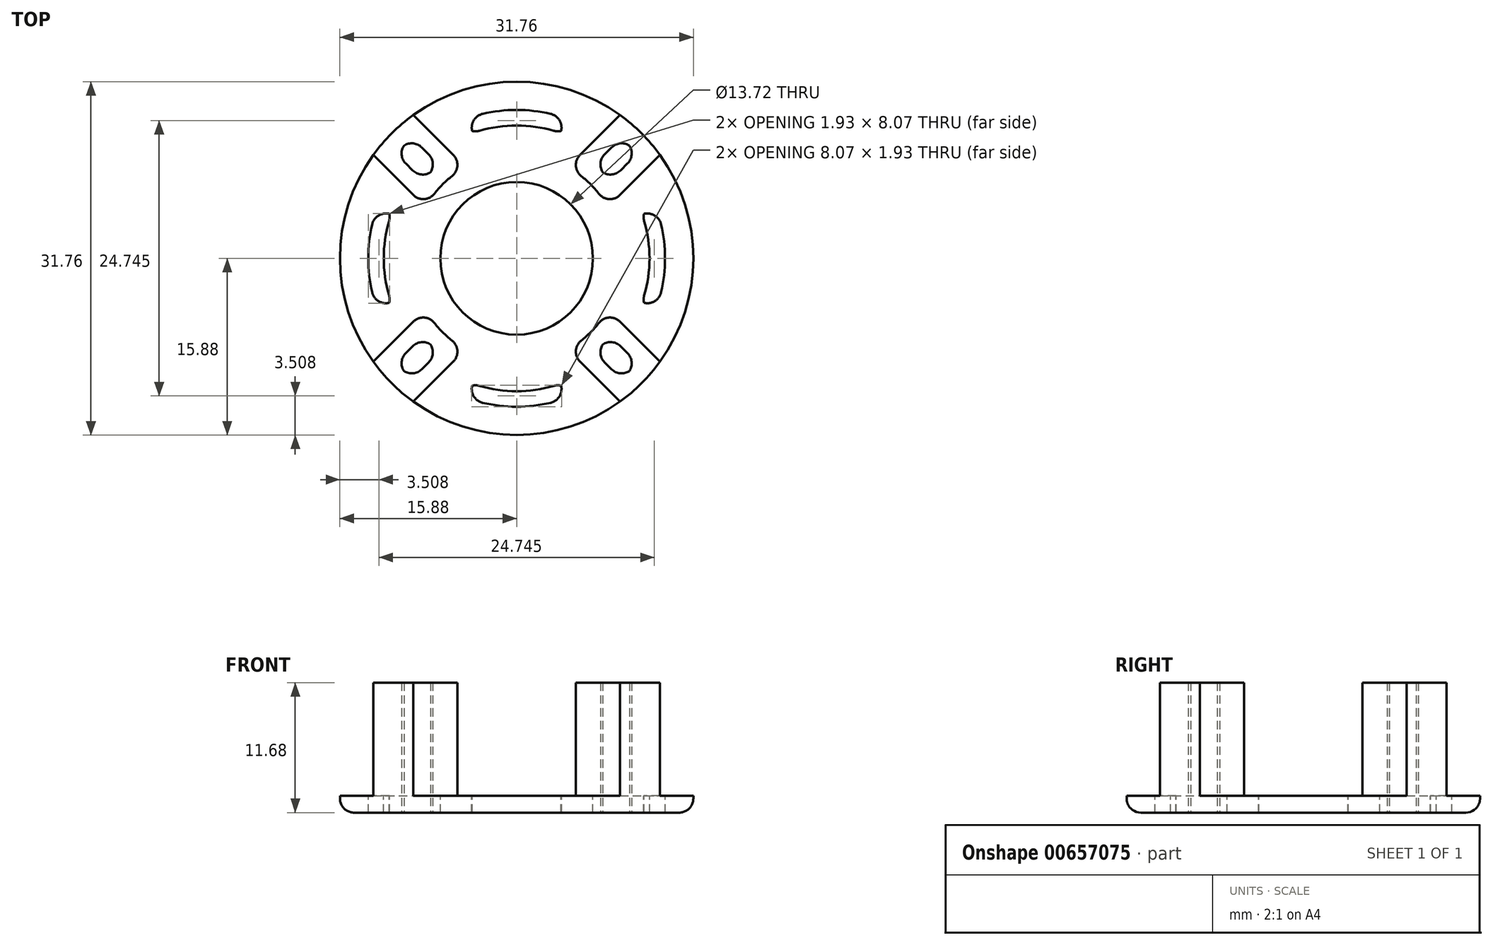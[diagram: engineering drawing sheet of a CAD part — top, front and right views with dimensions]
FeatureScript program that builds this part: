
annotation { "Feature Type Name" : "Feature", "Feature Type Description" : "" }
export const myFeature = defineFeature(function(context is Context, id is Id, definition is map)
    precondition{}
    {
        {
            var Q0;
            Q0=qCreatedBy(makeId("Top.planeOp"),FACE);
            var sketch = newSketch(context, id + "F0", { "sketchPlane" : qUnion([Q0])});
            skCircle(sketch, "E0", {"center": v(0, 0) * mm, "radius": 15.88 * mm});
            skSolve(sketch);
        }
        {
            var Q0;
            Q0=qSketchRegion(id+"F0",true);
            extrude(context, id + "F1", {"entities" : qUnion([Q0]), "depth" : 1.52 * mm, "offsetDistance" : 25.4 * mm});
        }
        {
            var Q0;
            Q0=makeQuery(id+"F1.opExtrude","CAP_FACE",FACE,{"disambiguationData":[OSD([sQuery(id+"F0.wireOp",EDGE,"E0")])],"isStart":false});
            var sketch = newSketch(context, id + "F2", { "sketchPlane" : qUnion([Q0])});
            skArc(sketch, "E1", {"start": v(-8.2, 4.6) * mm, "mid": v(-9.4, 0) * mm, "end": v(-8.2, -4.6) * mm, "construction": true});
            skArc(sketch, "E2", {"start": v(-4.6, 8.2) * mm, "mid": v(-6.65, 6.65) * mm, "end": v(-8.2, 4.6) * mm});
            skArc(sketch, "E3", {"start": v(4.6, 8.2) * mm, "mid": v(0, 9.4) * mm, "end": v(-4.6, 8.2) * mm, "construction": true});
            skArc(sketch, "E4", {"start": v(8.2, 4.6) * mm, "mid": v(6.65, 6.65) * mm, "end": v(4.6, 8.2) * mm});
            skArc(sketch, "E5", {"start": v(8.2, -4.6) * mm, "mid": v(9.4, 0) * mm, "end": v(8.2, 4.6) * mm, "construction": true});
            skArc(sketch, "E6", {"start": v(4.6, -8.2) * mm, "mid": v(6.65, -6.65) * mm, "end": v(8.2, -4.6) * mm});
            skArc(sketch, "E7", {"start": v(-4.6, -8.2) * mm, "mid": v(0, -9.4) * mm, "end": v(4.6, -8.2) * mm, "construction": true});
            skArc(sketch, "E8", {"start": v(-8.2, -4.6) * mm, "mid": v(-6.65, -6.65) * mm, "end": v(-4.6, -8.2) * mm});
            skArc(sketch, "E9", {"start": v(-12.88, -9.28) * mm, "mid": v(-11.23, -11.23) * mm, "end": v(-9.28, -12.88) * mm});
            skArc(sketch, "E10", {"start": v(-12.88, 9.28) * mm, "mid": v(-15.87, 0) * mm, "end": v(-12.88, -9.28) * mm, "construction": true});
            skArc(sketch, "E11", {"start": v(-9.28, 12.88) * mm, "mid": v(-11.23, 11.23) * mm, "end": v(-12.88, 9.28) * mm});
            skArc(sketch, "E12", {"start": v(9.28, 12.88) * mm, "mid": v(0, 15.88) * mm, "end": v(-9.28, 12.88) * mm, "construction": true});
            skArc(sketch, "E13", {"start": v(12.88, 9.28) * mm, "mid": v(11.23, 11.23) * mm, "end": v(9.28, 12.88) * mm});
            skArc(sketch, "E14", {"start": v(12.88, -9.28) * mm, "mid": v(15.88, 0) * mm, "end": v(12.88, 9.28) * mm, "construction": true});
            skArc(sketch, "E15", {"start": v(9.28, -12.88) * mm, "mid": v(11.23, -11.23) * mm, "end": v(12.88, -9.28) * mm});
            skArc(sketch, "E16", {"start": v(-9.28, -12.88) * mm, "mid": v(0, -15.88) * mm, "end": v(9.28, -12.88) * mm, "construction": true});
            skLineSegment(sketch, "E17", {"start": v(-12.88, 9.28) * mm, "end": v(-8.2, 4.6) * mm});
            skLineSegment(sketch, "E18", {"start": v(-4.6, 8.2) * mm, "end": v(-9.28, 12.88) * mm});
            skLineSegment(sketch, "E19", {"start": v(4.6, 8.2) * mm, "end": v(9.28, 12.88) * mm});
            skLineSegment(sketch, "E20", {"start": v(8.2, 4.6) * mm, "end": v(12.88, 9.28) * mm});
            skLineSegment(sketch, "E21", {"start": v(4.6, -8.2) * mm, "end": v(9.28, -12.88) * mm});
            skLineSegment(sketch, "E22", {"start": v(8.2, -4.6) * mm, "end": v(12.88, -9.28) * mm});
            skLineSegment(sketch, "E23", {"start": v(-9.28, -12.88) * mm, "end": v(-4.6, -8.2) * mm});
            skLineSegment(sketch, "E24", {"start": v(-12.88, -9.28) * mm, "end": v(-8.2, -4.6) * mm});
            skLineSegment(sketch, "E25", {"start": v(8.2, 4.6) * mm, "end": v(0, 4.6) * mm, "construction": true});
            skLineSegment(sketch, "E26", {"start": v(4.6, 8.2) * mm, "end": v(4.6, 0) * mm, "construction": true});
            skSolve(sketch);
        }
        {
            var Q0;
            Q0 = qSketchRegion(id + "F2", true);
            extrude(context, id + "F3", {"entities" : qUnion([Q0]), "operationType" : NewBodyOperationType.ADD, "depth" : 10.16 * mm, "offsetDistance" : 25.4 * mm});
        }
        {
            var Q0;
            Q0=makeQuery(id+"F1.opExtrude","CAP_FACE",FACE,{"disambiguationData":[OSD([sQuery(id+"F0.wireOp",EDGE,"E0")])],"isStart":false});
            var sketch = newSketch(context, id + "F4", { "sketchPlane" : qUnion([Q0])});
            skCircle(sketch, "E27", {"center": v(0, 0) * mm, "radius": 6.86 * mm});
            skArc(sketch, "E28", {"start": v(-12.31, 5.13) * mm, "mid": v(-13.34, 0) * mm, "end": v(-12.31, -5.13) * mm});
            skArc(sketch, "E29", {"start": v(-12.31, -5.13) * mm, "mid": v(-9.43, -9.43) * mm, "end": v(-5.13, -12.31) * mm, "construction": true});
            skArc(sketch, "E30", {"start": v(-11.23, -4.05) * mm, "mid": v(-8.44, -8.44) * mm, "end": v(-4.05, -11.23) * mm, "construction": true});
            skArc(sketch, "E31", {"start": v(-11.23, 4.05) * mm, "mid": v(-11.94, 0) * mm, "end": v(-11.23, -4.05) * mm});
            skArc(sketch, "E32", {"start": v(-5.13, 12.31) * mm, "mid": v(-9.43, 9.43) * mm, "end": v(-12.31, 5.13) * mm, "construction": true});
            skArc(sketch, "E33", {"start": v(-4.05, 11.23) * mm, "mid": v(-8.44, 8.44) * mm, "end": v(-11.23, 4.05) * mm, "construction": true});
            skArc(sketch, "E34", {"start": v(4.05, 11.23) * mm, "mid": v(0, 11.94) * mm, "end": v(-4.05, 11.23) * mm});
            skArc(sketch, "E35", {"start": v(5.13, 12.31) * mm, "mid": v(0, 13.33) * mm, "end": v(-5.13, 12.31) * mm});
            skArc(sketch, "E36", {"start": v(12.31, 5.13) * mm, "mid": v(9.43, 9.43) * mm, "end": v(5.13, 12.31) * mm, "construction": true});
            skArc(sketch, "E37", {"start": v(11.23, 4.05) * mm, "mid": v(8.44, 8.44) * mm, "end": v(4.05, 11.23) * mm, "construction": true});
            skArc(sketch, "E38", {"start": v(11.23, -4.05) * mm, "mid": v(11.94, 0) * mm, "end": v(11.23, 4.05) * mm});
            skArc(sketch, "E39", {"start": v(12.31, -5.13) * mm, "mid": v(13.33, 0) * mm, "end": v(12.31, 5.13) * mm});
            skArc(sketch, "E40", {"start": v(5.13, -12.31) * mm, "mid": v(9.43, -9.43) * mm, "end": v(12.31, -5.13) * mm, "construction": true});
            skArc(sketch, "E41", {"start": v(4.05, -11.23) * mm, "mid": v(8.44, -8.44) * mm, "end": v(11.23, -4.05) * mm, "construction": true});
            skArc(sketch, "E42", {"start": v(-4.05, -11.23) * mm, "mid": v(0, -11.94) * mm, "end": v(4.05, -11.23) * mm});
            skArc(sketch, "E43", {"start": v(-5.13, -12.31) * mm, "mid": v(0, -13.34) * mm, "end": v(5.13, -12.31) * mm});
            skLineSegment(sketch, "E44", {"start": v(-12.31, -5.13) * mm, "end": v(-11.23, -4.05) * mm});
            skLineSegment(sketch, "E45", {"start": v(-12.31, 5.13) * mm, "end": v(-11.23, 4.05) * mm});
            skLineSegment(sketch, "E46", {"start": v(-5.13, 12.31) * mm, "end": v(-4.05, 11.23) * mm});
            skLineSegment(sketch, "E47", {"start": v(4.05, 11.23) * mm, "end": v(5.13, 12.31) * mm});
            skLineSegment(sketch, "E48", {"start": v(11.23, 4.05) * mm, "end": v(12.31, 5.13) * mm});
            skLineSegment(sketch, "E49", {"start": v(11.23, -4.05) * mm, "end": v(12.31, -5.13) * mm});
            skLineSegment(sketch, "E50", {"start": v(4.05, -11.23) * mm, "end": v(5.13, -12.31) * mm});
            skLineSegment(sketch, "E51", {"start": v(-5.13, -12.31) * mm, "end": v(-4.05, -11.23) * mm});
            skSolve(sketch);
        }
        {
            var Q0;
            Q0 = qSketchRegion(id + "F4", true);
            var Q1;
            Q1=makeQuery(id+"F1.opExtrude","SWEPT_BODY",BODY,{"disambiguationData":[OSD([sQuery(id+"F0.wireOp",EDGE,"E0")])]});
            extrude(context, id + "F5", {"entities" : qUnion([Q0]), "operationType" : NewBodyOperationType.REMOVE, "endBound" : BoundingType.UP_TO_BODY, "oppositeDirection" : true, "depth" : 25.4 * mm, "endBoundEntityBody" : qUnion([Q1]), "offsetDistance" : 25.4 * mm});
        }
        {
            var Q0;
            Q0=makeQuery(id+"F5.boolean.opBoolean","COPY",EDGE,{"derivedFrom":makeQuery(id+"F5.opExtrude","SWEPT_EDGE",EDGE,{"disambiguationData":[OSD([sQuery(id+"F4.wireOp",EDGE,"E28"),sQuery(id+"F4.wireOp",EDGE,"E45")])]})});
            var Q1;
            Q1=makeQuery(id+"F5.boolean.opBoolean","COPY",EDGE,{"derivedFrom":makeQuery(id+"F5.opExtrude","SWEPT_EDGE",EDGE,{"disambiguationData":[OSD([sQuery(id+"F4.wireOp",EDGE,"E31"),sQuery(id+"F4.wireOp",EDGE,"E45")])]})});
            var Q2;
            Q2=makeQuery(id+"F5.boolean.opBoolean","COPY",EDGE,{"derivedFrom":makeQuery(id+"F5.opExtrude","SWEPT_EDGE",EDGE,{"disambiguationData":[OSD([sQuery(id+"F4.wireOp",EDGE,"E31"),sQuery(id+"F4.wireOp",EDGE,"E44")])]})});
            var Q3;
            Q3=makeQuery(id+"F5.boolean.opBoolean","COPY",EDGE,{"derivedFrom":makeQuery(id+"F5.opExtrude","SWEPT_EDGE",EDGE,{"disambiguationData":[OSD([sQuery(id+"F4.wireOp",EDGE,"E28"),sQuery(id+"F4.wireOp",EDGE,"E44")])]})});
            var Q4;
            Q4=makeQuery(id+"F5.boolean.opBoolean","COPY",EDGE,{"derivedFrom":makeQuery(id+"F5.opExtrude","SWEPT_EDGE",EDGE,{"disambiguationData":[OSD([sQuery(id+"F4.wireOp",EDGE,"E34"),sQuery(id+"F4.wireOp",EDGE,"E46")])]})});
            var Q5;
            Q5=makeQuery(id+"F5.boolean.opBoolean","COPY",EDGE,{"derivedFrom":makeQuery(id+"F5.opExtrude","SWEPT_EDGE",EDGE,{"disambiguationData":[OSD([sQuery(id+"F4.wireOp",EDGE,"E34"),sQuery(id+"F4.wireOp",EDGE,"E47")])]})});
            var Q6;
            Q6=makeQuery(id+"F5.boolean.opBoolean","COPY",EDGE,{"derivedFrom":makeQuery(id+"F5.opExtrude","SWEPT_EDGE",EDGE,{"disambiguationData":[OSD([sQuery(id+"F4.wireOp",EDGE,"E35"),sQuery(id+"F4.wireOp",EDGE,"E46")])]})});
            var Q7;
            Q7=makeQuery(id+"F5.boolean.opBoolean","COPY",EDGE,{"derivedFrom":makeQuery(id+"F5.opExtrude","SWEPT_EDGE",EDGE,{"disambiguationData":[OSD([sQuery(id+"F4.wireOp",EDGE,"E35"),sQuery(id+"F4.wireOp",EDGE,"E47")])]})});
            var Q8;
            Q8=makeQuery(id+"F5.boolean.opBoolean","COPY",EDGE,{"derivedFrom":makeQuery(id+"F5.opExtrude","SWEPT_EDGE",EDGE,{"disambiguationData":[OSD([sQuery(id+"F4.wireOp",EDGE,"E42"),sQuery(id+"F4.wireOp",EDGE,"E50")])]})});
            var Q9;
            Q9=makeQuery(id+"F5.boolean.opBoolean","COPY",EDGE,{"derivedFrom":makeQuery(id+"F5.opExtrude","SWEPT_EDGE",EDGE,{"disambiguationData":[OSD([sQuery(id+"F4.wireOp",EDGE,"E42"),sQuery(id+"F4.wireOp",EDGE,"E51")])]})});
            var Q10;
            Q10=makeQuery(id+"F5.boolean.opBoolean","COPY",EDGE,{"derivedFrom":makeQuery(id+"F5.opExtrude","SWEPT_EDGE",EDGE,{"disambiguationData":[OSD([sQuery(id+"F4.wireOp",EDGE,"E39"),sQuery(id+"F4.wireOp",EDGE,"E48")])]})});
            var Q11;
            Q11=makeQuery(id+"F5.boolean.opBoolean","COPY",EDGE,{"derivedFrom":makeQuery(id+"F5.opExtrude","SWEPT_EDGE",EDGE,{"disambiguationData":[OSD([sQuery(id+"F4.wireOp",EDGE,"E43"),sQuery(id+"F4.wireOp",EDGE,"E50")])]})});
            var Q12;
            Q12=makeQuery(id+"F5.boolean.opBoolean","COPY",EDGE,{"derivedFrom":makeQuery(id+"F5.opExtrude","SWEPT_EDGE",EDGE,{"disambiguationData":[OSD([sQuery(id+"F4.wireOp",EDGE,"E43"),sQuery(id+"F4.wireOp",EDGE,"E51")])]})});
            var Q13;
            Q13=makeQuery(id+"F5.boolean.opBoolean","COPY",EDGE,{"derivedFrom":makeQuery(id+"F5.opExtrude","SWEPT_EDGE",EDGE,{"disambiguationData":[OSD([sQuery(id+"F4.wireOp",EDGE,"E38"),sQuery(id+"F4.wireOp",EDGE,"E48")])]})});
            var Q14;
            Q14=makeQuery(id+"F5.boolean.opBoolean","COPY",EDGE,{"derivedFrom":makeQuery(id+"F5.opExtrude","SWEPT_EDGE",EDGE,{"disambiguationData":[OSD([sQuery(id+"F4.wireOp",EDGE,"E38"),sQuery(id+"F4.wireOp",EDGE,"E49")])]})});
            var Q15;
            Q15=makeQuery(id+"F5.boolean.opBoolean","COPY",EDGE,{"derivedFrom":makeQuery(id+"F5.opExtrude","SWEPT_EDGE",EDGE,{"disambiguationData":[OSD([sQuery(id+"F4.wireOp",EDGE,"E39"),sQuery(id+"F4.wireOp",EDGE,"E49")])]})});
            var Q16;
            Q16=makeQuery(id+"F3.opExtrude","SWEPT_EDGE",EDGE,{"disambiguationData":[OSD([sQuery(id+"F2.wireOp",EDGE,"E8"),sQuery(id+"F2.wireOp",EDGE,"E23")])]});
            var Q17;
            Q17=makeQuery(id+"F3.opExtrude","SWEPT_EDGE",EDGE,{"disambiguationData":[OSD([sQuery(id+"F2.wireOp",EDGE,"E8"),sQuery(id+"F2.wireOp",EDGE,"E24")])]});
            var Q18;
            Q18=makeQuery(id+"F3.opExtrude","SWEPT_EDGE",EDGE,{"disambiguationData":[OSD([sQuery(id+"F2.wireOp",EDGE,"E2"),sQuery(id+"F2.wireOp",EDGE,"E17")])]});
            var Q19;
            Q19=makeQuery(id+"F3.opExtrude","SWEPT_EDGE",EDGE,{"disambiguationData":[OSD([sQuery(id+"F2.wireOp",EDGE,"E2"),sQuery(id+"F2.wireOp",EDGE,"E18")])]});
            var Q20;
            Q20=makeQuery(id+"F3.opExtrude","SWEPT_EDGE",EDGE,{"disambiguationData":[OSD([sQuery(id+"F2.wireOp",EDGE,"E6"),sQuery(id+"F2.wireOp",EDGE,"E22")])]});
            var Q21;
            Q21=makeQuery(id+"F3.opExtrude","SWEPT_EDGE",EDGE,{"disambiguationData":[OSD([sQuery(id+"F2.wireOp",EDGE,"E4"),sQuery(id+"F2.wireOp",EDGE,"E20")])]});
            var Q22;
            Q22=makeQuery(id+"F3.opExtrude","SWEPT_EDGE",EDGE,{"disambiguationData":[OSD([sQuery(id+"F2.wireOp",EDGE,"E4"),sQuery(id+"F2.wireOp",EDGE,"E19")])]});
            var Q23;
            Q23=makeQuery(id+"F3.opExtrude","SWEPT_EDGE",EDGE,{"disambiguationData":[OSD([sQuery(id+"F2.wireOp",EDGE,"E6"),sQuery(id+"F2.wireOp",EDGE,"E21")])]});
            var Q24;
            Q24=makeQuery(id+"F1.opExtrude","CAP_EDGE",EDGE,{"disambiguationData":[OSD([sQuery(id+"F0.wireOp",EDGE,"E0")])],"isStart":true});
            fillet(context, id + "F6", {"entities" : qUnion([Q0, Q1, Q2, Q3, Q4, Q5, Q6, Q7, Q8, Q9, Q10, Q11, Q12, Q13, Q14, Q15, Q16, Q17, Q18, Q19, Q20, Q21, Q22, Q23, Q24]), "radius" : 1.27 * mm, "tangentPropagation" : true, "allowEdgeOverflow" : false});
        }
        {
            var Q0;
            Q0=makeQuery(id+"F3.opExtrude","CAP_FACE",FACE,{"disambiguationData":[OSD([sQuery(id+"F2.wireOp",EDGE,"E8"),sQuery(id+"F2.wireOp",EDGE,"E9"),sQuery(id+"F2.wireOp",EDGE,"E23"),sQuery(id+"F2.wireOp",EDGE,"E24")])],"isStart":false});
            var Q1;
            Q1=makeQuery(id+"F3.opExtrude","CAP_FACE",FACE,{"disambiguationData":[OSD([sQuery(id+"F2.wireOp",EDGE,"E2"),sQuery(id+"F2.wireOp",EDGE,"E11"),sQuery(id+"F2.wireOp",EDGE,"E17"),sQuery(id+"F2.wireOp",EDGE,"E18")])],"isStart":false});
            var Q2;
            Q2=makeQuery(id+"F3.opExtrude","CAP_FACE",FACE,{"disambiguationData":[OSD([sQuery(id+"F2.wireOp",EDGE,"E6"),sQuery(id+"F2.wireOp",EDGE,"E15"),sQuery(id+"F2.wireOp",EDGE,"E21"),sQuery(id+"F2.wireOp",EDGE,"E22")])],"isStart":false});
            var Q3;
            Q3=makeQuery(id+"F3.opExtrude","CAP_FACE",FACE,{"disambiguationData":[OSD([sQuery(id+"F2.wireOp",EDGE,"E4"),sQuery(id+"F2.wireOp",EDGE,"E13"),sQuery(id+"F2.wireOp",EDGE,"E19"),sQuery(id+"F2.wireOp",EDGE,"E20")])],"isStart":false});
            shell(context, id + "F7", {"entities" : qUnion([Q0, Q1, Q2, Q3]), "thickness" : 1.52 * mm});
        }
        {
            var Q0;
            Q0=makeQuery(id+"F7.opShell","OFFSET_FACE",FACE,{"disambiguationData":[OSD([sQuery(id+"F0.wireOp",EDGE,"E0")]),OD(3.0)]});
            var Q1;
            Q1=makeQuery(id+"F7.opShell","OFFSET_FACE",FACE,{"disambiguationData":[OSD([sQuery(id+"F0.wireOp",EDGE,"E0")]),OD(0.0)]});
            var Q2;
            Q2=makeQuery(id+"F7.opShell","OFFSET_FACE",FACE,{"disambiguationData":[OSD([sQuery(id+"F0.wireOp",EDGE,"E0")]),OD(2.0)]});
            var Q3;
            Q3=makeQuery(id+"F7.opShell","OFFSET_FACE",FACE,{"disambiguationData":[OSD([sQuery(id+"F0.wireOp",EDGE,"E0")]),OD(1.0)]});
            var Q4;
            Q4=makeQuery(id+"F1.opExtrude","CAP_FACE",FACE,{"disambiguationData":[OSD([sQuery(id+"F0.wireOp",EDGE,"E0")])],"isStart":true});
            extrude(context, id + "F8", {"entities" : qUnion([Q0, Q1, Q2, Q3]), "operationType" : NewBodyOperationType.REMOVE, "endBound" : BoundingType.UP_TO_SURFACE, "oppositeDirection" : true, "depth" : 25.4 * mm, "endBoundEntityFace" : qUnion([Q4]), "offsetDistance" : 25.4 * mm});
        }
        {
            var Q0;
            Q0=makeQuery(id+"F3.opExtrude","CAP_EDGE",EDGE,{"disambiguationData":[OSD([sQuery(id+"F2.wireOp",EDGE,"E4")])],"isStart":true});
            var Q1;
            Q1=makeQuery(id+"F3.opExtrude","CAP_EDGE",EDGE,{"disambiguationData":[OSD([sQuery(id+"F2.wireOp",EDGE,"E2")])],"isStart":true});
            var Q2;
            Q2=makeQuery(id+"F3.opExtrude","CAP_EDGE",EDGE,{"disambiguationData":[OSD([sQuery(id+"F2.wireOp",EDGE,"E8")])],"isStart":true});
            var Q3;
            Q3=makeQuery(id+"F3.opExtrude","CAP_EDGE",EDGE,{"disambiguationData":[OSD([sQuery(id+"F2.wireOp",EDGE,"E6")])],"isStart":true});
            var Q4;
            {var subQ0=sQuery(id+"F2.wireOp",EDGE,"E17");var subQ1=sQuery(id+"F2.wireOp",EDGE,"E2");Q4=makeQuery(id+"F8.boolean.opBoolean","MERGE",EDGE,{"derivedFrom":[makeQuery(id+"F7.opShell","OFFSET_EDGE",EDGE,{"disambiguationData":[OSD([subQ1,subQ0])]}),makeQuery(id+"F8.opExtrude","SWEPT_EDGE",EDGE,{"disambiguationData":[OSD([sQuery(id+"F0.wireOp",EDGE,"E0"),subQ1,subQ0])]})]});}
            var Q5;
            {var subQ0=sQuery(id+"F2.wireOp",EDGE,"E18");var subQ1=sQuery(id+"F2.wireOp",EDGE,"E2");Q5=makeQuery(id+"F8.boolean.opBoolean","MERGE",EDGE,{"derivedFrom":[makeQuery(id+"F7.opShell","OFFSET_EDGE",EDGE,{"disambiguationData":[OSD([subQ1,subQ0])]}),makeQuery(id+"F8.opExtrude","SWEPT_EDGE",EDGE,{"disambiguationData":[OSD([sQuery(id+"F0.wireOp",EDGE,"E0"),subQ1,subQ0])]})]});}
            var Q6;
            {var subQ0=sQuery(id+"F2.wireOp",EDGE,"E18");var subQ1=sQuery(id+"F2.wireOp",EDGE,"E11");var subQ2=sQuery(id+"F0.wireOp",EDGE,"E0");Q6=makeQuery(id+"F8.boolean.opBoolean","MERGE",EDGE,{"derivedFrom":[makeQuery(id+"F7.opShell","OFFSET_EDGE",EDGE,{"disambiguationData":[OSD([subQ2,subQ1,subQ0])]}),makeQuery(id+"F8.opExtrude","SWEPT_EDGE",EDGE,{"disambiguationData":[OSD([subQ2,sQuery(id+"F2.wireOp",EDGE,"E9"),subQ1,sQuery(id+"F2.wireOp",EDGE,"E13"),sQuery(id+"F2.wireOp",EDGE,"E15"),subQ0])]})]});}
            var Q7;
            {var subQ0=sQuery(id+"F2.wireOp",EDGE,"E17");var subQ1=sQuery(id+"F2.wireOp",EDGE,"E11");var subQ2=sQuery(id+"F0.wireOp",EDGE,"E0");Q7=makeQuery(id+"F8.boolean.opBoolean","MERGE",EDGE,{"derivedFrom":[makeQuery(id+"F7.opShell","OFFSET_EDGE",EDGE,{"disambiguationData":[OSD([subQ2,subQ1,subQ0])]}),makeQuery(id+"F8.opExtrude","SWEPT_EDGE",EDGE,{"disambiguationData":[OSD([subQ2,sQuery(id+"F2.wireOp",EDGE,"E9"),subQ1,sQuery(id+"F2.wireOp",EDGE,"E13"),sQuery(id+"F2.wireOp",EDGE,"E15"),subQ0])]})]});}
            var Q8;
            {var subQ0=sQuery(id+"F2.wireOp",EDGE,"E24");var subQ1=sQuery(id+"F2.wireOp",EDGE,"E8");Q8=makeQuery(id+"F8.boolean.opBoolean","MERGE",EDGE,{"derivedFrom":[makeQuery(id+"F7.opShell","OFFSET_EDGE",EDGE,{"disambiguationData":[OSD([subQ1,subQ0])]}),makeQuery(id+"F8.opExtrude","SWEPT_EDGE",EDGE,{"disambiguationData":[OSD([sQuery(id+"F0.wireOp",EDGE,"E0"),subQ1,subQ0])]})]});}
            var Q9;
            {var subQ0=sQuery(id+"F2.wireOp",EDGE,"E24");var subQ1=sQuery(id+"F2.wireOp",EDGE,"E9");var subQ2=sQuery(id+"F0.wireOp",EDGE,"E0");Q9=makeQuery(id+"F8.boolean.opBoolean","MERGE",EDGE,{"derivedFrom":[makeQuery(id+"F7.opShell","OFFSET_EDGE",EDGE,{"disambiguationData":[OSD([subQ2,subQ1,subQ0])]}),makeQuery(id+"F8.opExtrude","SWEPT_EDGE",EDGE,{"disambiguationData":[OSD([subQ2,subQ1,sQuery(id+"F2.wireOp",EDGE,"E11"),sQuery(id+"F2.wireOp",EDGE,"E13"),sQuery(id+"F2.wireOp",EDGE,"E15"),subQ0])]})]});}
            var Q10;
            {var subQ0=sQuery(id+"F2.wireOp",EDGE,"E23");var subQ1=sQuery(id+"F2.wireOp",EDGE,"E9");var subQ2=sQuery(id+"F0.wireOp",EDGE,"E0");Q10=makeQuery(id+"F8.boolean.opBoolean","MERGE",EDGE,{"derivedFrom":[makeQuery(id+"F7.opShell","OFFSET_EDGE",EDGE,{"disambiguationData":[OSD([subQ2,subQ1,subQ0])]}),makeQuery(id+"F8.opExtrude","SWEPT_EDGE",EDGE,{"disambiguationData":[OSD([subQ2,subQ1,sQuery(id+"F2.wireOp",EDGE,"E11"),sQuery(id+"F2.wireOp",EDGE,"E13"),sQuery(id+"F2.wireOp",EDGE,"E15"),subQ0])]})]});}
            var Q11;
            {var subQ0=sQuery(id+"F2.wireOp",EDGE,"E23");var subQ1=sQuery(id+"F2.wireOp",EDGE,"E8");Q11=makeQuery(id+"F8.boolean.opBoolean","MERGE",EDGE,{"derivedFrom":[makeQuery(id+"F7.opShell","OFFSET_EDGE",EDGE,{"disambiguationData":[OSD([subQ1,subQ0])]}),makeQuery(id+"F8.opExtrude","SWEPT_EDGE",EDGE,{"disambiguationData":[OSD([sQuery(id+"F0.wireOp",EDGE,"E0"),subQ1,subQ0])]})]});}
            var Q12;
            {var subQ0=sQuery(id+"F2.wireOp",EDGE,"E20");var subQ1=sQuery(id+"F2.wireOp",EDGE,"E13");var subQ2=sQuery(id+"F0.wireOp",EDGE,"E0");Q12=makeQuery(id+"F8.boolean.opBoolean","MERGE",EDGE,{"derivedFrom":[makeQuery(id+"F7.opShell","OFFSET_EDGE",EDGE,{"disambiguationData":[OSD([subQ2,subQ1,subQ0])]}),makeQuery(id+"F8.opExtrude","SWEPT_EDGE",EDGE,{"disambiguationData":[OSD([subQ2,sQuery(id+"F2.wireOp",EDGE,"E9"),sQuery(id+"F2.wireOp",EDGE,"E11"),subQ1,sQuery(id+"F2.wireOp",EDGE,"E15"),subQ0])]})]});}
            var Q13;
            {var subQ0=sQuery(id+"F2.wireOp",EDGE,"E22");var subQ1=sQuery(id+"F2.wireOp",EDGE,"E15");var subQ2=sQuery(id+"F0.wireOp",EDGE,"E0");Q13=makeQuery(id+"F8.boolean.opBoolean","MERGE",EDGE,{"derivedFrom":[makeQuery(id+"F7.opShell","OFFSET_EDGE",EDGE,{"disambiguationData":[OSD([subQ2,subQ1,subQ0])]}),makeQuery(id+"F8.opExtrude","SWEPT_EDGE",EDGE,{"disambiguationData":[OSD([subQ2,sQuery(id+"F2.wireOp",EDGE,"E9"),sQuery(id+"F2.wireOp",EDGE,"E11"),sQuery(id+"F2.wireOp",EDGE,"E13"),subQ1,subQ0])]})]});}
            var Q14;
            {var subQ0=sQuery(id+"F2.wireOp",EDGE,"E19");var subQ1=sQuery(id+"F2.wireOp",EDGE,"E4");Q14=makeQuery(id+"F8.boolean.opBoolean","MERGE",EDGE,{"derivedFrom":[makeQuery(id+"F7.opShell","OFFSET_EDGE",EDGE,{"disambiguationData":[OSD([subQ1,subQ0])]}),makeQuery(id+"F8.opExtrude","SWEPT_EDGE",EDGE,{"disambiguationData":[OSD([sQuery(id+"F0.wireOp",EDGE,"E0"),subQ1,subQ0])]})]});}
            var Q15;
            {var subQ0=sQuery(id+"F2.wireOp",EDGE,"E21");var subQ1=sQuery(id+"F2.wireOp",EDGE,"E6");Q15=makeQuery(id+"F8.boolean.opBoolean","MERGE",EDGE,{"derivedFrom":[makeQuery(id+"F7.opShell","OFFSET_EDGE",EDGE,{"disambiguationData":[OSD([subQ1,subQ0])]}),makeQuery(id+"F8.opExtrude","SWEPT_EDGE",EDGE,{"disambiguationData":[OSD([sQuery(id+"F0.wireOp",EDGE,"E0"),subQ1,subQ0])]})]});}
            var Q16;
            {var subQ0=sQuery(id+"F2.wireOp",EDGE,"E19");var subQ1=sQuery(id+"F2.wireOp",EDGE,"E13");var subQ2=sQuery(id+"F0.wireOp",EDGE,"E0");Q16=makeQuery(id+"F8.boolean.opBoolean","MERGE",EDGE,{"derivedFrom":[makeQuery(id+"F7.opShell","OFFSET_EDGE",EDGE,{"disambiguationData":[OSD([subQ2,subQ1,subQ0])]}),makeQuery(id+"F8.opExtrude","SWEPT_EDGE",EDGE,{"disambiguationData":[OSD([subQ2,sQuery(id+"F2.wireOp",EDGE,"E9"),sQuery(id+"F2.wireOp",EDGE,"E11"),subQ1,sQuery(id+"F2.wireOp",EDGE,"E15"),subQ0])]})]});}
            var Q17;
            {var subQ0=sQuery(id+"F2.wireOp",EDGE,"E22");var subQ1=sQuery(id+"F2.wireOp",EDGE,"E6");Q17=makeQuery(id+"F8.boolean.opBoolean","MERGE",EDGE,{"derivedFrom":[makeQuery(id+"F7.opShell","OFFSET_EDGE",EDGE,{"disambiguationData":[OSD([subQ1,subQ0])]}),makeQuery(id+"F8.opExtrude","SWEPT_EDGE",EDGE,{"disambiguationData":[OSD([sQuery(id+"F0.wireOp",EDGE,"E0"),subQ1,subQ0])]})]});}
            var Q18;
            {var subQ0=sQuery(id+"F2.wireOp",EDGE,"E21");var subQ1=sQuery(id+"F2.wireOp",EDGE,"E15");var subQ2=sQuery(id+"F0.wireOp",EDGE,"E0");Q18=makeQuery(id+"F8.boolean.opBoolean","MERGE",EDGE,{"derivedFrom":[makeQuery(id+"F7.opShell","OFFSET_EDGE",EDGE,{"disambiguationData":[OSD([subQ2,subQ1,subQ0])]}),makeQuery(id+"F8.opExtrude","SWEPT_EDGE",EDGE,{"disambiguationData":[OSD([subQ2,sQuery(id+"F2.wireOp",EDGE,"E9"),sQuery(id+"F2.wireOp",EDGE,"E11"),sQuery(id+"F2.wireOp",EDGE,"E13"),subQ1,subQ0])]})]});}
            var Q19;
            {var subQ0=sQuery(id+"F2.wireOp",EDGE,"E20");var subQ1=sQuery(id+"F2.wireOp",EDGE,"E4");Q19=makeQuery(id+"F8.boolean.opBoolean","MERGE",EDGE,{"derivedFrom":[makeQuery(id+"F7.opShell","OFFSET_EDGE",EDGE,{"disambiguationData":[OSD([subQ1,subQ0])]}),makeQuery(id+"F8.opExtrude","SWEPT_EDGE",EDGE,{"disambiguationData":[OSD([sQuery(id+"F0.wireOp",EDGE,"E0"),subQ1,subQ0])]})]});}
            fillet(context, id + "F9", {"entities" : qUnion([Q0, Q1, Q2, Q3, Q4, Q5, Q6, Q7, Q8, Q9, Q10, Q11, Q12, Q13, Q14, Q15, Q16, Q17, Q18, Q19]), "radius" : 1.27 * mm, "tangentPropagation" : true, "allowEdgeOverflow" : false});
        }
    });
